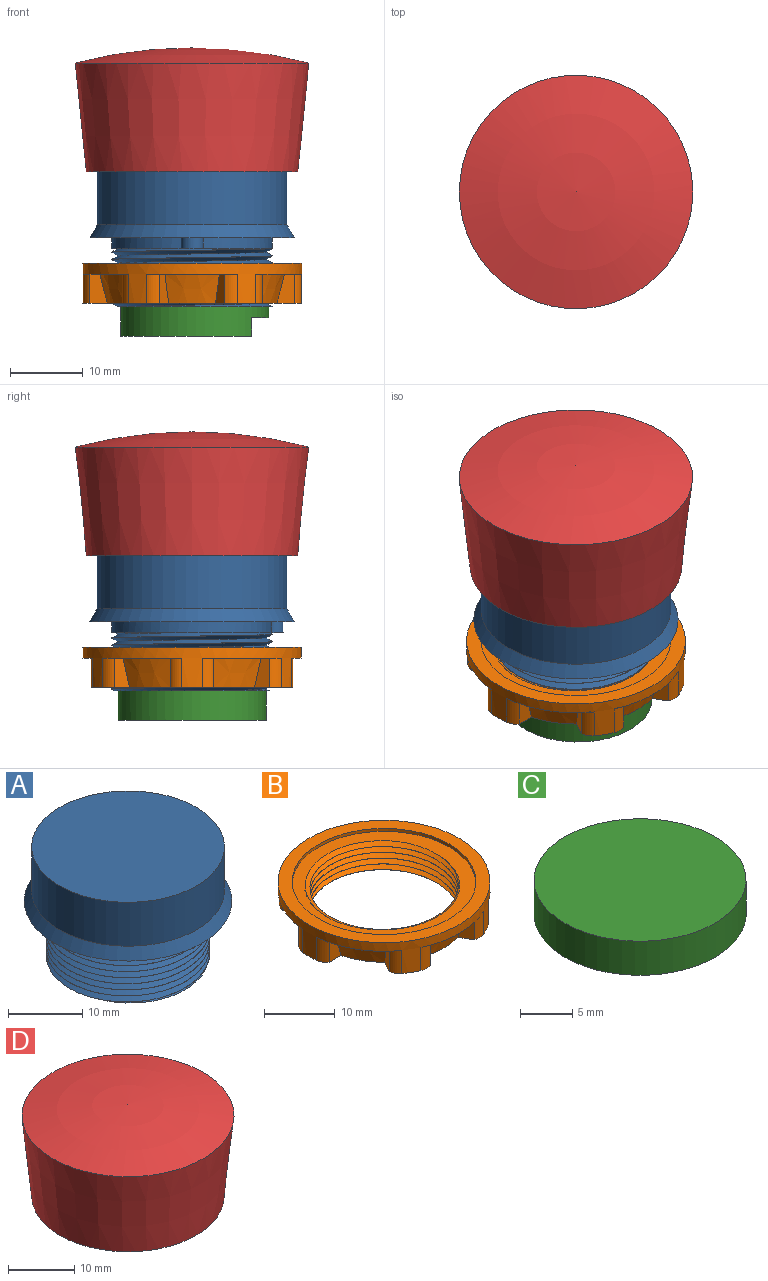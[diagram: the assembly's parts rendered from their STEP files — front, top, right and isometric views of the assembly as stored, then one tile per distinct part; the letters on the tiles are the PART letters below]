
ASSEMBLY  parts=4 mates=3
PART A: 10 faces, bbox 28.8x28.8x20 mm
  f0: plane 21.96x21.95mm, normal (0,0,-1), area 351.2mm2, adj f1,f2,f3
  f1: cylinder r=11mm len=22mm, axis (0,0,1), area 98.4mm2, adj f0,f2,f3,f4,f8,f9
  f2: bspline ~25.4x22mm, area 532.6mm2, adj f0,f1,f3,f4
  f3: bspline ~25.4x22mm, area 532.9mm2, adj f0,f1,f2,f4
  f4: plane 24.3x22.8mm, normal (0,0,-1), area 32.6mm2, adj f1,f2,f3,f9
  f5: cylinder r=13mm len=26mm, axis (0,0,-1), area 592.2mm2, adj f6,f7
  f6: plane 26x26mm, normal (0,0,1), area 530.9mm2, adj f5
  f7: cone r=14mm half-angle=29.7deg, axis (0,0,-1), area 171mm2, adj f5,f8
  f8: plane 28x28mm, normal (0,0,-1), area 232mm2, adj f1,f7,f9
  f9: cylinder r=1.5mm len=3mm, axis (0,0,1), area 7.4mm2, adj f1,f4,f8
PART B: 44 faces, bbox 30x30x6.2 mm
  f0: bspline ~26.23x22.71mm, area 339.7mm2, adj f1,f2,f16,f42
  f1: bspline ~26.23x22.71mm, area 339.7mm2, adj f0,f2,f16,f42
  f2: cylinder r=10.5mm len=21mm, axis (0,0,1), area 3.7mm2, adj f0,f1,f16,f42
  f3: plane 30x30mm, normal (0,0,1), area 175.9mm2, adj f15,f43
  f4: cone r=13mm half-angle=14deg, axis (0,0,1), area 29mm2, adj f14,f16,f20,f41
  f5: plane 12.49x2.55mm, normal (0,0,-1), area 18mm2, adj f6,f15,f35,f37,f38,f40
  f6: cone r=13mm half-angle=14deg, axis (0,0,1), area 29mm2, adj f5,f16,f37,f40
  f7: plane 10.82x6.25mm, normal (0,0,-1), area 18mm2, adj f8,f15,f31,f33,f34,f36
  f8: cone r=13mm half-angle=14deg, axis (0,0,1), area 29mm2, adj f7,f16,f33,f36
  f9: plane 10.82x6.25mm, normal (0,0,-1), area 18mm2, adj f10,f15,f27,f29,f30,f32
  f10: cone r=13mm half-angle=14deg, axis (0,0,1), area 29mm2, adj f9,f16,f29,f32
  f11: plane 12.49x2.55mm, normal (0,0,-1), area 18mm2, adj f13,f15,f23,f25,f26,f28
  f12: plane 10.82x6.25mm, normal (0,0,-1), area 18mm2, adj f15,f17,f19,f21,f22,f24
  f13: cone r=13mm half-angle=14deg, axis (0,0,1), area 29mm2, adj f11,f16,f25,f28
  f14: plane 10.82x6.25mm, normal (0,0,-1), area 18mm2, adj f4,f15,f18,f20,f39,f41
  f15: cylinder r=15mm len=30mm, axis (0,0,1), area 209.1mm2, adj f3,f5,f7,f9,f11,f12,f14,f16
  f16: plane 30x27.61mm, normal (0,0,-1), area 181.8mm2, adj f0,f1,f2,f4,f6,f8,f10,f13
  f17: cone r=13mm half-angle=14deg, axis (0,0,1), area 29mm2, adj f12,f16,f21,f24
  f18: cylinder r=2.55mm len=4mm, axis (0,0,1), area 7.6mm2, adj f14,f15,f16,f20
  f19: cylinder r=2.55mm len=4mm, axis (0,0,1), area 7.6mm2, adj f12,f15,f16,f21
  f20: plane 4.01x2.39mm, normal (0,-1,0), area 7.5mm2, adj f4,f14,f16,f18
  f21: plane 4.01x2.39mm, normal (0,1,0), area 7.5mm2, adj f12,f16,f17,f19
  f22: cylinder r=2.55mm len=4mm, axis (0,0,1), area 7.6mm2, adj f12,f15,f16,f24
  f23: cylinder r=2.55mm len=4mm, axis (0,0,1), area 7.6mm2, adj f11,f15,f16,f25
  f24: plane 4.01x2.07mm, normal (-0.87,-0.5,0), area 7.5mm2, adj f12,f16,f17,f22
  f25: plane 4.01x2.07mm, normal (0.87,0.5,0), area 7.5mm2, adj f11,f13,f16,f23
  f26: cylinder r=2.55mm len=4mm, axis (0,0,1), area 7.6mm2, adj f11,f15,f16,f28
  f27: cylinder r=2.55mm len=4mm, axis (0,0,1), area 7.6mm2, adj f9,f15,f16,f29
  f28: plane 4.01x2.07mm, normal (-0.87,0.5,0), area 7.5mm2, adj f11,f13,f16,f26
  f29: plane 4.01x2.07mm, normal (0.87,-0.5,0), area 7.5mm2, adj f9,f10,f16,f27
  f30: cylinder r=2.55mm len=4mm, axis (0,0,1), area 7.6mm2, adj f9,f15,f16,f32
  f31: cylinder r=2.55mm len=4mm, axis (0,0,1), area 7.6mm2, adj f7,f15,f16,f33
  f32: plane 4.01x2.39mm, normal (0,1,0), area 7.5mm2, adj f9,f10,f16,f30
  f33: plane 4.01x2.39mm, normal (0,-1,0), area 7.5mm2, adj f7,f8,f16,f31
  f34: cylinder r=2.55mm len=4mm, axis (0,0,1), area 7.6mm2, adj f7,f15,f16,f36
  f35: cylinder r=2.55mm len=4mm, axis (0,0,1), area 7.6mm2, adj f5,f15,f16,f37
  f36: plane 4.01x2.07mm, normal (0.87,0.5,0), area 7.5mm2, adj f7,f8,f16,f34
  f37: plane 4.01x2.07mm, normal (-0.87,-0.5,0), area 7.5mm2, adj f5,f6,f16,f35
  f38: cylinder r=2.55mm len=4mm, axis (0,0,1), area 7.6mm2, adj f5,f15,f16,f40
  f39: cylinder r=2.55mm len=4mm, axis (0,0,1), area 7.6mm2, adj f14,f15,f16,f41
  f40: plane 4.01x2.07mm, normal (0.87,-0.5,0), area 7.5mm2, adj f5,f6,f16,f38
  f41: plane 4.01x2.07mm, normal (-0.87,0.5,0), area 7.5mm2, adj f4,f14,f16,f39
  f42: plane 26x26mm, normal (0,0,1), area 155.8mm2, adj f0,f1,f2,f43
  f43: cylinder r=13mm len=26mm, axis (0,0,1), area 40.8mm2, adj f3,f42
PART C: 7 faces, bbox 20.3x20.3x4 mm
  f0: plane 20.3x17.95mm, normal (0,0,-1), area 277.4mm2, adj f1,f3,f4,f5
  f1: cylinder r=10.15mm len=20.3mm, axis (0,0,1), area 219.8mm2, adj f0,f2,f3,f5,f6
  f2: plane 20.3x20.3mm, normal (0,0,1), area 323.7mm2, adj f1
  f3: plane 2.5x1.95mm, normal (0,1,0), area 4.9mm2, adj f0,f1,f4,f6
  f4: plane 13x2.5mm, normal (1,0,0), area 32.5mm2, adj f0,f3,f5,f6
  f5: plane 2.5x1.95mm, normal (0,-1,0), area 4.9mm2, adj f0,f1,f4,f6
  f6: plane 13x4.3mm, normal (0,0,-1), area 46.2mm2, adj f1,f3,f4,f5
PART D: 3 faces, bbox 32x32x17 mm
  f0: cone r=14.5mm half-angle=5.7deg, axis (0,0,1), area 1437.3mm2, adj f1,f2
  f1: sphere r=62.72mm, area 817.8mm2, adj f0
  f2: plane 29x29mm, normal (0,0,-1), area 660.5mm2, adj f0
PLACE A at identity fixed
PLACE B t=(0,0,-3.5)mm
PLACE C t=(0.36,-0.01,0)mm
PLACE D at identity
MATE fastened C.f1 <-> A.f0  axis (0,0,1) through (0.36,-0.01,-9.5)mm
MATE slider D.f0 <-> A.f5  axis (0,0,-1) through (0,0,9)mm
MATE fastened B.f2 <-> A.f1  axis (0,0,1) through (0,0,-3.5)mm
